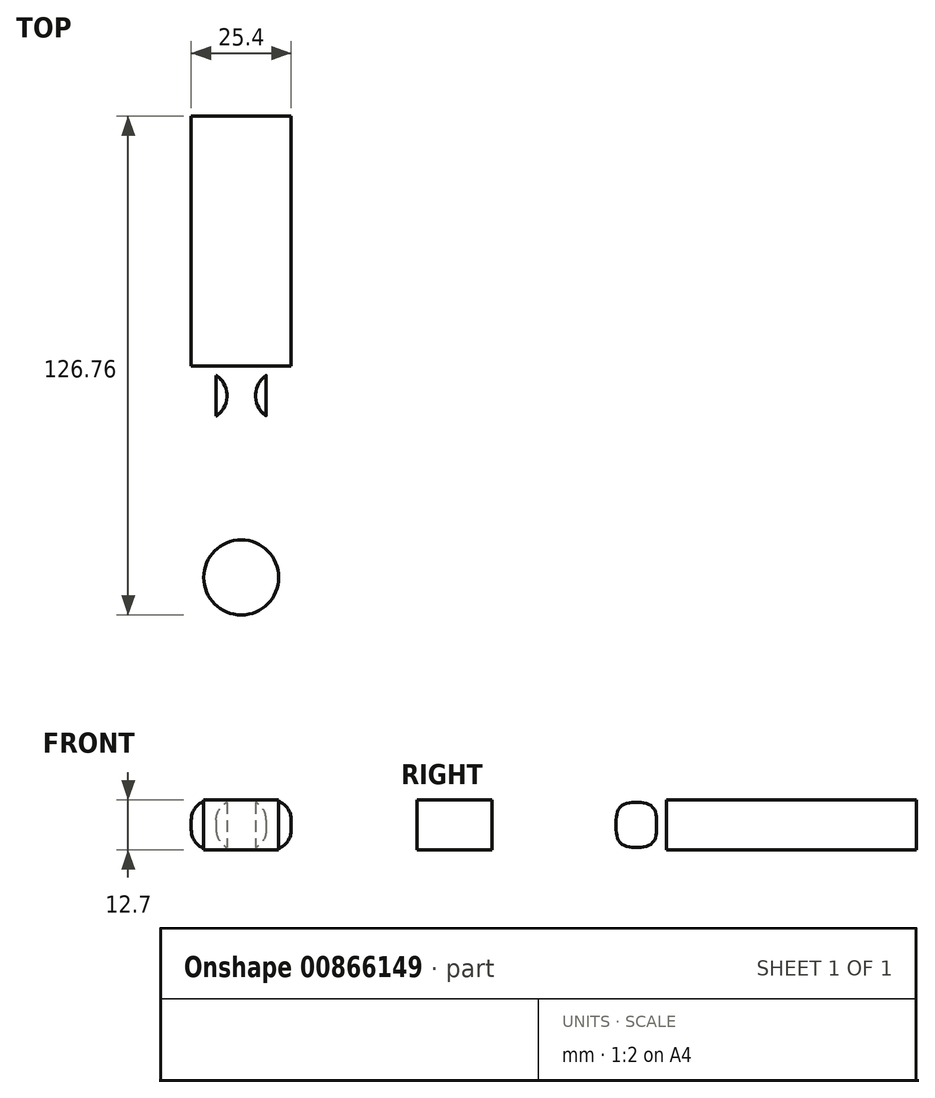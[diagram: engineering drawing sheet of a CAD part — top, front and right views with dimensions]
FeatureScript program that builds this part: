
annotation { "Feature Type Name" : "Feature", "Feature Type Description" : "" }
export const myFeature = defineFeature(function(context is Context, id is Id, definition is map)
    precondition{}
    {
        {
            var Q0;
            Q0=qCreatedBy(makeId("Top.planeOp"),FACE);
            var sketch = newSketch(context, id + "F0", { "sketchPlane" : qUnion([Q0])});
            skLineSegment(sketch, "E0", {"start": v(0, 0) * mm, "end": v(0, 50.8) * mm});
            skLineSegment(sketch, "E1", {"start": v(0, 50.8) * mm, "end": v(12.7, 50.8) * mm});
            skLineSegment(sketch, "E2.MirrorCS", {"start": v(0, 50.8) * mm, "end": v(-12.7, 50.8) * mm});
            skLineSegment(sketch, "E3.bottom", {"start": v(-12.7, 50.8) * mm, "end": v(12.7, 50.8) * mm});
            skLineSegment(sketch, "E3.top", {"start": v(-12.7, -12.7) * mm, "end": v(12.7, -12.7) * mm});
            skLineSegment(sketch, "E3.left", {"start": v(-12.7, 50.8) * mm, "end": v(-12.7, -12.7) * mm});
            skLineSegment(sketch, "E3.right", {"start": v(12.7, 50.8) * mm, "end": v(12.7, -12.7) * mm});
            skLineSegment(sketch, "E4", {"start": v(0, 0) * mm, "end": v(0, -56.9) * mm});
            skPoint(sketch, "E4.endSnap0", {"position": v(0, -12.7) * mm});
            skPoint(sketch, "E5", {"position": v(-6.35, -12.7) * mm});
            skPoint(sketch, "E6.MirrorP", {"position": v(6.35, -12.7) * mm});
            skLineSegment(sketch, "E7.bottom", {"start": v(-6.35, -12.7) * mm, "end": v(6.35, -12.7) * mm});
            skLineSegment(sketch, "E7.top", {"start": v(-6.35, -56.9) * mm, "end": v(6.35, -56.9) * mm});
            skLineSegment(sketch, "E7.left", {"start": v(-6.35, -12.7) * mm, "end": v(-6.35, -56.9) * mm});
            skLineSegment(sketch, "E7.right", {"start": v(6.35, -12.7) * mm, "end": v(6.35, -56.9) * mm});
            skCircle(sketch, "E8", {"center": v(0, -66.43) * mm, "radius": 9.53 * mm});
            skCircle(sketch, "E9", {"center": v(-9.83, -20.26) * mm, "radius": 6.21 * mm});
            skCircle(sketch, "E10.MirrorC", {"center": v(9.83, -20.26) * mm, "radius": 6.21 * mm});
            skSolve(sketch);
        }
        {
            var Q0;
            {var subQ5=sQuery(id+"F0.wireOp",EDGE,"E0");Q0=makeQuery(id+"F0.imprint","IMPRINT",FACE,{"disambiguationData":[TD([[makeQuery(id+"F0.imprint","IMPRINT",EDGE,{"derivedFrom":subQ5}),1.0]])]});}
            var Q1;
            {var subQ5=sQuery(id+"F0.wireOp",EDGE,"E0");Q1=makeQuery(id+"F0.imprint","IMPRINT",FACE,{"disambiguationData":[TD([[makeQuery(id+"F0.imprint","IMPRINT",EDGE,{"derivedFrom":subQ5}),-1.0]])]});}
            var Q2;
            {var subQ3=sQuery(id+"F0.wireOp",EDGE,"E7.right");var subQ7=sQuery(id+"F0.wireOp",EDGE,"1ndjm9f4-UWwl-oF27-z4Oz-XoTAVXRKPaTq");var subQ16=makeQuery(id+"F0.imprint","INTERSECT",VERTEX,{"disambiguationData":[OD(1.0)],"derivedFrom":[subQ3,subQ7]});Q2=makeQuery(id+"F0.imprint","IMPRINT",FACE,{"disambiguationData":[TD([[makeQuery(id+"F0.imprint","IMPRINT",EDGE,{"disambiguationData":[TD([[subQ16,-1.0]])],"derivedFrom":subQ3}),-1.0]])]});}
            var Q3;
            {var subQ3=sQuery(id+"F0.wireOp",EDGE,"E7.left");var subQ8=sQuery(id+"F0.wireOp",EDGE,"ec5fa23c-6829-49b9-86cd-1809c006e7280.MirrorC");var subQ12=makeQuery(id+"F0.imprint","INTERSECT",VERTEX,{"disambiguationData":[OD(1.0)],"derivedFrom":[subQ3,subQ8]});Q3=makeQuery(id+"F0.imprint","IMPRINT",FACE,{"disambiguationData":[TD([[makeQuery(id+"F0.imprint","IMPRINT",EDGE,{"disambiguationData":[TD([[subQ12,-1.0]])],"derivedFrom":subQ3}),1.0]])]});}
            var Q4;
            Q4=makeQuery(id+"F0.imprint","IMPRINT",FACE,{"disambiguationData":[TD([[makeQuery(id+"F0.imprint","IMPRINT",EDGE,{"derivedFrom":sQuery(id+"F0.wireOp",EDGE,"E8")}),1.0]])]});
            extrude(context, id + "F1", {"entities" : qUnion([Q0, Q1, Q2, Q3, Q4]), "depth" : 12.7 * mm, "offsetDistance" : 25.4 * mm});
        }
        {
            var Q0;
            {var subQ0=sQuery(id+"F0.wireOp",EDGE,"E7.left");Q0=makeQuery(id+"F1.opExtrude","CAP_EDGE",EDGE,{"disambiguationData":[OSD([subQ0]),TDD([makeQuery(id+"F0.imprint","IMPRINT",EDGE,{"disambiguationData":[TD([[makeQuery(id+"F0.imprint","INTERSECT",VERTEX,{"disambiguationData":[OD(1.0)],"derivedFrom":[subQ0,sQuery(id+"F0.wireOp",EDGE,"ec5fa23c-6829-49b9-86cd-1809c006e7280.MirrorC")]}),-1.0]])],"derivedFrom":subQ0})])],"isStart":false});}
            var Q1;
            {var subQ0=sQuery(id+"F0.wireOp",EDGE,"E7.right");Q1=makeQuery(id+"F1.opExtrude","CAP_EDGE",EDGE,{"disambiguationData":[OSD([subQ0]),TDD([makeQuery(id+"F0.imprint","IMPRINT",EDGE,{"disambiguationData":[TD([[makeQuery(id+"F0.imprint","INTERSECT",VERTEX,{"disambiguationData":[OD(1.0)],"derivedFrom":[subQ0,sQuery(id+"F0.wireOp",EDGE,"1ndjm9f4-UWwl-oF27-z4Oz-XoTAVXRKPaTq")]}),-1.0]])],"derivedFrom":subQ0})])],"isStart":false});}
            var Q2;
            {var subQ0=sQuery(id+"F0.wireOp",EDGE,"E7.right");Q2=makeQuery(id+"F1.opExtrude","CAP_EDGE",EDGE,{"disambiguationData":[OSD([subQ0]),TDD([makeQuery(id+"F0.imprint","IMPRINT",EDGE,{"disambiguationData":[TD([[makeQuery(id+"F0.imprint","INTERSECT",VERTEX,{"disambiguationData":[OD(0.0)],"derivedFrom":[subQ0,sQuery(id+"F0.wireOp",EDGE,"1ndjm9f4-UWwl-oF27-z4Oz-XoTAVXRKPaTq")]}),1.0]])],"derivedFrom":subQ0})])],"isStart":true});}
            var Q3;
            {var subQ0=sQuery(id+"F0.wireOp",EDGE,"E7.left");Q3=makeQuery(id+"F1.opExtrude","CAP_EDGE",EDGE,{"disambiguationData":[OSD([subQ0]),TDD([makeQuery(id+"F0.imprint","IMPRINT",EDGE,{"disambiguationData":[TD([[makeQuery(id+"F0.imprint","INTERSECT",VERTEX,{"disambiguationData":[OD(0.0)],"derivedFrom":[subQ0,sQuery(id+"F0.wireOp",EDGE,"ec5fa23c-6829-49b9-86cd-1809c006e7280.MirrorC")]}),1.0]])],"derivedFrom":subQ0})])],"isStart":true});}
            fillet(context, id + "F2", {"entities" : qUnion([Q0, Q1, Q2, Q3]), "radius" : 5.08 * mm, "tangentPropagation" : true, "allowEdgeOverflow" : false});
        }
        {
            var Q0;
            Q0=makeQuery(id+"F1.opExtrude","CAP_EDGE",EDGE,{"disambiguationData":[OSD([sQuery(id+"F0.wireOp",EDGE,"E3.right")])],"isStart":false});
            var Q1;
            Q1=makeQuery(id+"F1.opExtrude","CAP_EDGE",EDGE,{"disambiguationData":[OSD([sQuery(id+"F0.wireOp",EDGE,"E3.left")])],"isStart":false});
            var Q2;
            Q2=makeQuery(id+"F1.opExtrude","CAP_EDGE",EDGE,{"disambiguationData":[OSD([sQuery(id+"F0.wireOp",EDGE,"E3.left")])],"isStart":true});
            var Q3;
            Q3=makeQuery(id+"F1.opExtrude","CAP_EDGE",EDGE,{"disambiguationData":[OSD([sQuery(id+"F0.wireOp",EDGE,"E3.right")])],"isStart":true});
            fillet(context, id + "F3", {"entities" : qUnion([Q0, Q1, Q2, Q3]), "radius" : 5.08 * mm, "tangentPropagation" : true, "allowEdgeOverflow" : false});
        }
    });
